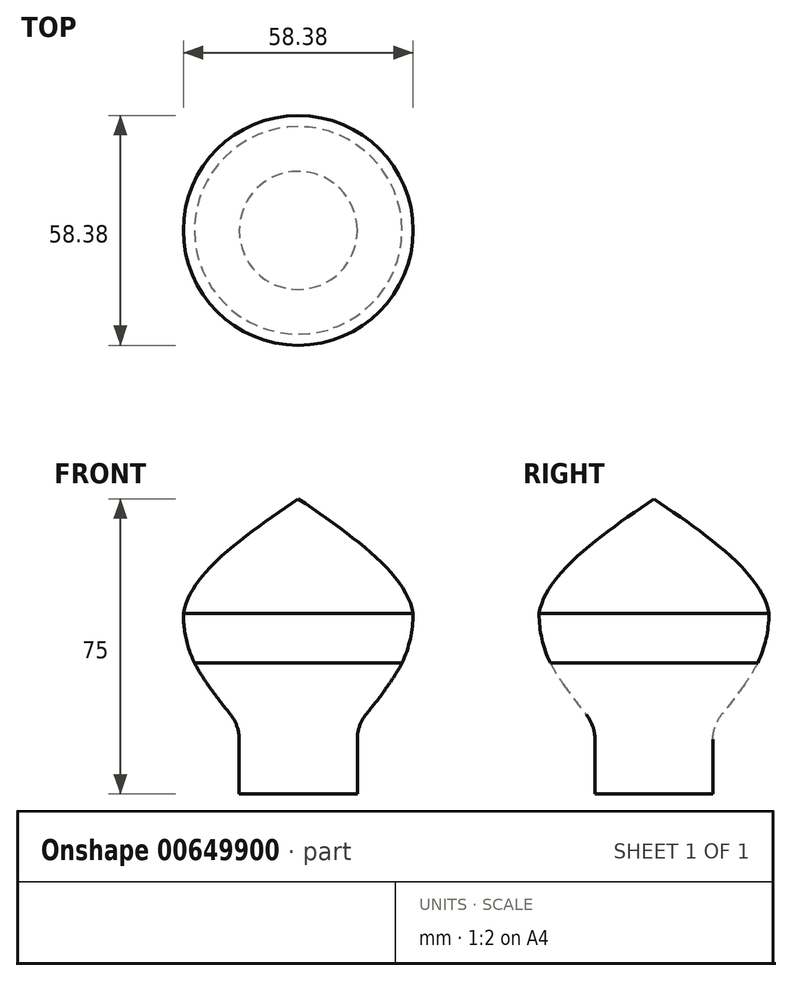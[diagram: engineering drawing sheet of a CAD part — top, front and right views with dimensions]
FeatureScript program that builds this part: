
annotation { "Feature Type Name" : "Feature", "Feature Type Description" : "" }
export const myFeature = defineFeature(function(context is Context, id is Id, definition is map)
    precondition{}
    {
        {
            var Q0;
            Q0=qCreatedBy(makeId("Front.planeOp"),FACE);
            var sketch = newSketch(context, id + "F0", { "sketchPlane" : qUnion([Q0])});
            skLineSegment(sketch, "E0", {"start": v(0, 0) * mm, "end": v(0, 75) * mm});
            skLineSegment(sketch, "E1.bottom", {"start": v(0, 0) * mm, "end": v(15, 0) * mm});
            skLineSegment(sketch, "E1.left", {"start": v(0, 0) * mm, "end": v(0, 17.43) * mm});
            skLineSegment(sketch, "E1.right", {"start": v(15, 0) * mm, "end": v(15, 13.9) * mm});
            skFitSpline(sketch, "E2", {"points": [v(15, 17.43) * mm, v(29.19, 45.81) * mm, v(0, 75) * mm], "startDerivative": vector(50.26, 62.14) * mm, "endDerivative": vector(-77.47, 53.19) * mm});
            skArc(sketch, "E3.trimOffspring", {"start": v(23.09, 27.95) * mm, "mid": v(26.2, 58.67) * mm, "end": v(0, 75) * mm});
            skArc(sketch, "E4.filletArc", {"start": v(17.2, 20.15) * mm, "mid": v(15.56, 17.22) * mm, "end": v(15, 13.9) * mm});
            skSolve(sketch);
        }
        {
            var Q0;
            {var subQ0=sQuery(id+"F0.wireOp",EDGE,"E0");Q0=makeQuery(id+"F0.imprint","IMPRINT",FACE,{"disambiguationData":[TD([[makeQuery(id+"F0.imprint","IMPRINT",EDGE,{"derivedFrom":subQ0}),-1.0]])]});}
            var Q1;
            Q1=sQuery(id+"F0.wireOp",EDGE,"E0");
            revolve(context, id + "F1", {"entities" : qUnion([Q0]), "axis" : qUnion([Q1]), "revolveType" : RevolveType.FULL});
        }
    });
